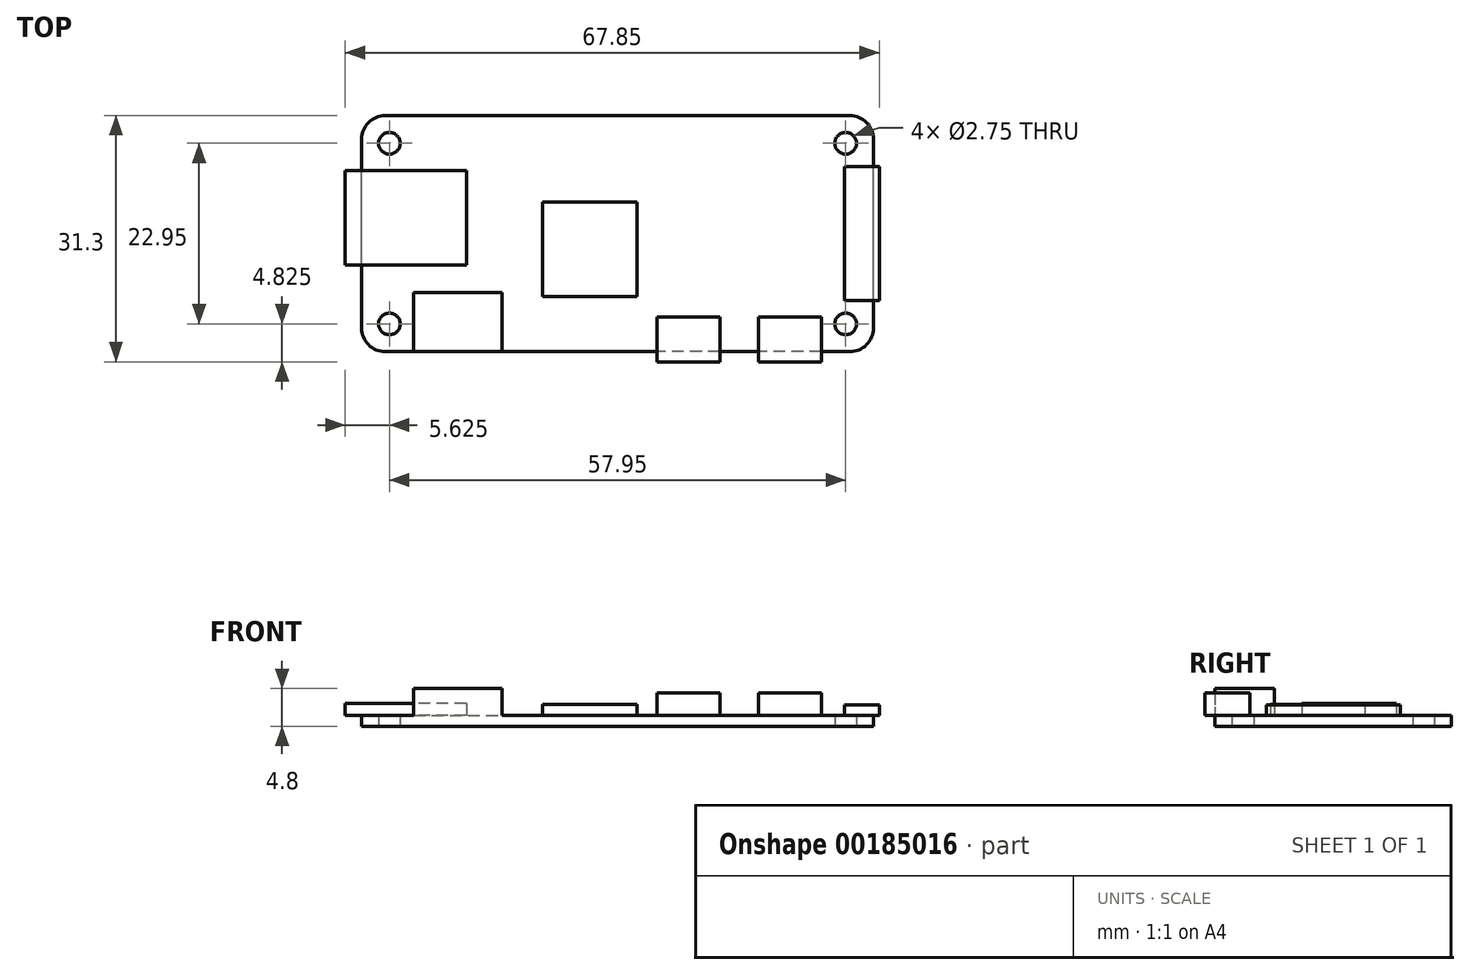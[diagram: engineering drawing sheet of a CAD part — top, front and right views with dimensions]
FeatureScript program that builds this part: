
annotation { "Feature Type Name" : "Feature", "Feature Type Description" : "" }
export const myFeature = defineFeature(function(context is Context, id is Id, definition is map)
    precondition{}
    {
        {
            var Q0;
            Q0=qCreatedBy(makeId("Top.planeOp"),FACE);
            var sketch = newSketch(context, id + "F0", { "sketchPlane" : qUnion([Q0])});
            skLineSegment(sketch, "E0.bottom", {"start": v(29.5, -15) * mm, "end": v(-29.5, -15) * mm});
            skLineSegment(sketch, "E0.top", {"start": v(29.5, 15) * mm, "end": v(-29.5, 15) * mm});
            skLineSegment(sketch, "E0.left", {"start": v(32.5, -12) * mm, "end": v(32.5, 12) * mm});
            skLineSegment(sketch, "E0.right", {"start": v(-32.5, -12) * mm, "end": v(-32.5, 12) * mm});
            skPoint(sketch, "E0.middle", {"position": v(0, 0) * mm});
            skCircle(sketch, "E1", {"center": v(-28.98, 11.47) * mm, "radius": 1.38 * mm});
            skCircle(sketch, "E2", {"center": v(28.98, 11.47) * mm, "radius": 1.38 * mm});
            skCircle(sketch, "E3", {"center": v(-28.98, -11.47) * mm, "radius": 1.38 * mm});
            skCircle(sketch, "E4", {"center": v(28.98, -11.47) * mm, "radius": 1.38 * mm});
            skPoint(sketch, "E5.visualSharp", {"position": v(-32.5, 15) * mm});
            skArc(sketch, "E5.filletArc", {"start": v(-29.5, 15) * mm, "mid": v(-31.62, 14.12) * mm, "end": v(-32.5, 12) * mm});
            skPoint(sketch, "E6.visualSharp", {"position": v(32.5, 15) * mm});
            skArc(sketch, "E6.filletArc", {"start": v(32.5, 12) * mm, "mid": v(31.62, 14.12) * mm, "end": v(29.5, 15) * mm});
            skPoint(sketch, "E7.visualSharp", {"position": v(32.5, -15) * mm});
            skArc(sketch, "E7.filletArc", {"start": v(29.5, -15) * mm, "mid": v(31.62, -14.12) * mm, "end": v(32.5, -12) * mm});
            skPoint(sketch, "E8.visualSharp", {"position": v(-32.5, -15) * mm});
            skArc(sketch, "E8.filletArc", {"start": v(-32.5, -12) * mm, "mid": v(-31.62, -14.12) * mm, "end": v(-29.5, -15) * mm});
            skSolve(sketch);
        }
        {
            var Q0;
            Q0 = qSketchRegion(id + "F0", true);
            extrude(context, id + "F1", {"entities" : qUnion([Q0]), "depth" : 1.4 * mm});
        }
        {
            var Q0;
            Q0=makeQuery(id+"F1.opExtrude","CAP_FACE",FACE,{"disambiguationData":[OSD([sQuery(id+"F0.wireOp",EDGE,"E0.bottom"),sQuery(id+"F0.wireOp",EDGE,"E0.top"),sQuery(id+"F0.wireOp",EDGE,"E0.left"),sQuery(id+"F0.wireOp",EDGE,"E0.right"),sQuery(id+"F0.wireOp",EDGE,"E1"),sQuery(id+"F0.wireOp",EDGE,"E2"),sQuery(id+"F0.wireOp",EDGE,"E3"),sQuery(id+"F0.wireOp",EDGE,"E4"),sQuery(id+"F0.wireOp",EDGE,"E5.filletArc"),sQuery(id+"F0.wireOp",EDGE,"E6.filletArc"),sQuery(id+"F0.wireOp",EDGE,"E7.filletArc"),sQuery(id+"F0.wireOp",EDGE,"E8.filletArc")])],"isStart":false});
            var sketch = newSketch(context, id + "F2", { "sketchPlane" : qUnion([Q0])});
            skLineSegment(sketch, "E9.bottom", {"start": v(2.5, -8) * mm, "end": v(-9.5, -8) * mm});
            skLineSegment(sketch, "E9.top", {"start": v(2.5, 4) * mm, "end": v(-9.5, 4) * mm});
            skLineSegment(sketch, "E9.left", {"start": v(2.5, -8) * mm, "end": v(2.5, 4) * mm});
            skLineSegment(sketch, "E9.right", {"start": v(-9.5, -8) * mm, "end": v(-9.5, 4) * mm});
            skPoint(sketch, "E9.middle", {"position": v(-3.5, -2) * mm});
            skLineSegment(sketch, "E10.bottom", {"start": v(33.25, -8.5) * mm, "end": v(28.85, -8.5) * mm});
            skLineSegment(sketch, "E10.top", {"start": v(33.25, 8.5) * mm, "end": v(28.85, 8.5) * mm});
            skLineSegment(sketch, "E10.left", {"start": v(33.25, -8.5) * mm, "end": v(33.25, 8.5) * mm});
            skLineSegment(sketch, "E10.right", {"start": v(28.85, -8.5) * mm, "end": v(28.85, 8.5) * mm});
            skPoint(sketch, "E10.middle", {"position": v(31.05, 0) * mm});
            skPoint(sketch, "E11", {"position": v(32.5, 0) * mm});
            skLineSegment(sketch, "E12.bottom", {"start": v(-19.2, -4) * mm, "end": v(-34.6, -4) * mm});
            skLineSegment(sketch, "E12.top", {"start": v(-19.2, 8) * mm, "end": v(-34.6, 8) * mm});
            skLineSegment(sketch, "E12.left", {"start": v(-19.2, -4) * mm, "end": v(-19.2, 8) * mm});
            skLineSegment(sketch, "E12.right", {"start": v(-34.6, -4) * mm, "end": v(-34.6, 8) * mm});
            skPoint(sketch, "E12.middle", {"position": v(-26.9, 2) * mm});
            skLineSegment(sketch, "E13.bottom", {"start": v(-25.9, -15) * mm, "end": v(-14.7, -15) * mm});
            skLineSegment(sketch, "E13.top", {"start": v(-25.9, -7.5) * mm, "end": v(-14.7, -7.5) * mm});
            skLineSegment(sketch, "E13.left", {"start": v(-25.9, -15) * mm, "end": v(-25.9, -7.5) * mm});
            skLineSegment(sketch, "E13.right", {"start": v(-14.7, -15) * mm, "end": v(-14.7, -7.5) * mm});
            skLineSegment(sketch, "E14.bottom", {"start": v(5, -16.3) * mm, "end": v(13, -16.3) * mm});
            skLineSegment(sketch, "E14.top", {"start": v(5, -10.6) * mm, "end": v(13, -10.6) * mm});
            skLineSegment(sketch, "E14.left", {"start": v(5, -16.3) * mm, "end": v(5, -10.6) * mm});
            skLineSegment(sketch, "E14.right", {"start": v(13, -16.3) * mm, "end": v(13, -10.6) * mm});
            skLineSegment(sketch, "E15.bottom", {"start": v(17.9, -16.3) * mm, "end": v(25.9, -16.3) * mm});
            skLineSegment(sketch, "E15.top", {"start": v(17.9, -10.6) * mm, "end": v(25.9, -10.6) * mm});
            skLineSegment(sketch, "E15.left", {"start": v(17.9, -16.3) * mm, "end": v(17.9, -10.6) * mm});
            skLineSegment(sketch, "E15.right", {"start": v(25.9, -16.3) * mm, "end": v(25.9, -10.6) * mm});
            skSolve(sketch);
        }
        {
            var Q0;
            Q0=makeQuery(id+"F2.imprint","IMPRINT",FACE,{"disambiguationData":[TD([[makeQuery(id+"F2.imprint","IMPRINT",EDGE,{"derivedFrom":sQuery(id+"F2.wireOp",EDGE,"E9.bottom")}),-1.0]])]});
            extrude(context, id + "F3", {"entities" : qUnion([Q0]), "operationType" : NewBodyOperationType.ADD, "depth" : 1.4 * mm});
        }
        {
            var Q0;
            Q0=makeQuery(id+"F2.imprint","IMPRINT",FACE,{"disambiguationData":[TD([[makeQuery(id+"F2.imprint","IMPRINT",EDGE,{"derivedFrom":sQuery(id+"F2.wireOp",EDGE,"E13.bottom")}),-1.0]])]});
            extrude(context, id + "F4", {"entities" : qUnion([Q0]), "operationType" : NewBodyOperationType.ADD, "depth" : (4.8 - 1.4) * mm});
        }
        {
            var Q0;
            {var subQ0=sQuery(id+"F2.wireOp",EDGE,"E14.top");Q0=makeQuery(id+"F2.imprint","IMPRINT",FACE,{"disambiguationData":[TD([[makeQuery(id+"F2.imprint","IMPRINT",EDGE,{"derivedFrom":subQ0}),-1.0]])]});}
            var Q1;
            {var subQ0=sQuery(id+"F2.wireOp",EDGE,"E15.top");Q1=makeQuery(id+"F2.imprint","IMPRINT",FACE,{"disambiguationData":[TD([[makeQuery(id+"F2.imprint","IMPRINT",EDGE,{"derivedFrom":subQ0}),-1.0]])]});}
            var Q2;
            {var subQ0=sQuery(id+"F2.wireOp",EDGE,"E15.bottom");Q2=makeQuery(id+"F2.imprint","IMPRINT",FACE,{"disambiguationData":[TD([[makeQuery(id+"F2.imprint","IMPRINT",EDGE,{"derivedFrom":subQ0}),1.0]])]});}
            var Q3;
            {var subQ0=sQuery(id+"F2.wireOp",EDGE,"E14.bottom");Q3=makeQuery(id+"F2.imprint","IMPRINT",FACE,{"disambiguationData":[TD([[makeQuery(id+"F2.imprint","IMPRINT",EDGE,{"derivedFrom":subQ0}),1.0]])]});}
            extrude(context, id + "F5", {"entities" : qUnion([Q0, Q1, Q2, Q3]), "operationType" : NewBodyOperationType.ADD, "depth" : (4.25 - 1.4) * mm});
        }
        {
            var Q0;
            {var subQ0=sQuery(id+"F2.wireOp",EDGE,"E10.right");Q0=makeQuery(id+"F2.imprint","IMPRINT",FACE,{"disambiguationData":[TD([[makeQuery(id+"F2.imprint","IMPRINT",EDGE,{"derivedFrom":subQ0}),-1.0]])]});}
            var Q1;
            {var subQ0=sQuery(id+"F2.wireOp",EDGE,"E10.left");Q1=makeQuery(id+"F2.imprint","IMPRINT",FACE,{"disambiguationData":[TD([[makeQuery(id+"F2.imprint","IMPRINT",EDGE,{"derivedFrom":subQ0}),1.0]])]});}
            extrude(context, id + "F6", {"entities" : qUnion([Q0, Q1]), "operationType" : NewBodyOperationType.ADD, "depth" : (2.75 - 1.4) * mm});
        }
        {
            var Q0;
            {var subQ0=sQuery(id+"F2.wireOp",EDGE,"E12.right");Q0=makeQuery(id+"F2.imprint","IMPRINT",FACE,{"disambiguationData":[TD([[makeQuery(id+"F2.imprint","IMPRINT",EDGE,{"derivedFrom":subQ0}),-1.0]])]});}
            var Q1;
            {var subQ0=sQuery(id+"F2.wireOp",EDGE,"E12.left");Q1=makeQuery(id+"F2.imprint","IMPRINT",FACE,{"disambiguationData":[TD([[makeQuery(id+"F2.imprint","IMPRINT",EDGE,{"derivedFrom":subQ0}),1.0]])]});}
            extrude(context, id + "F7", {"entities" : qUnion([Q0, Q1]), "operationType" : NewBodyOperationType.ADD, "depth" : (2.9 - 1.4) * mm});
        }
    });
